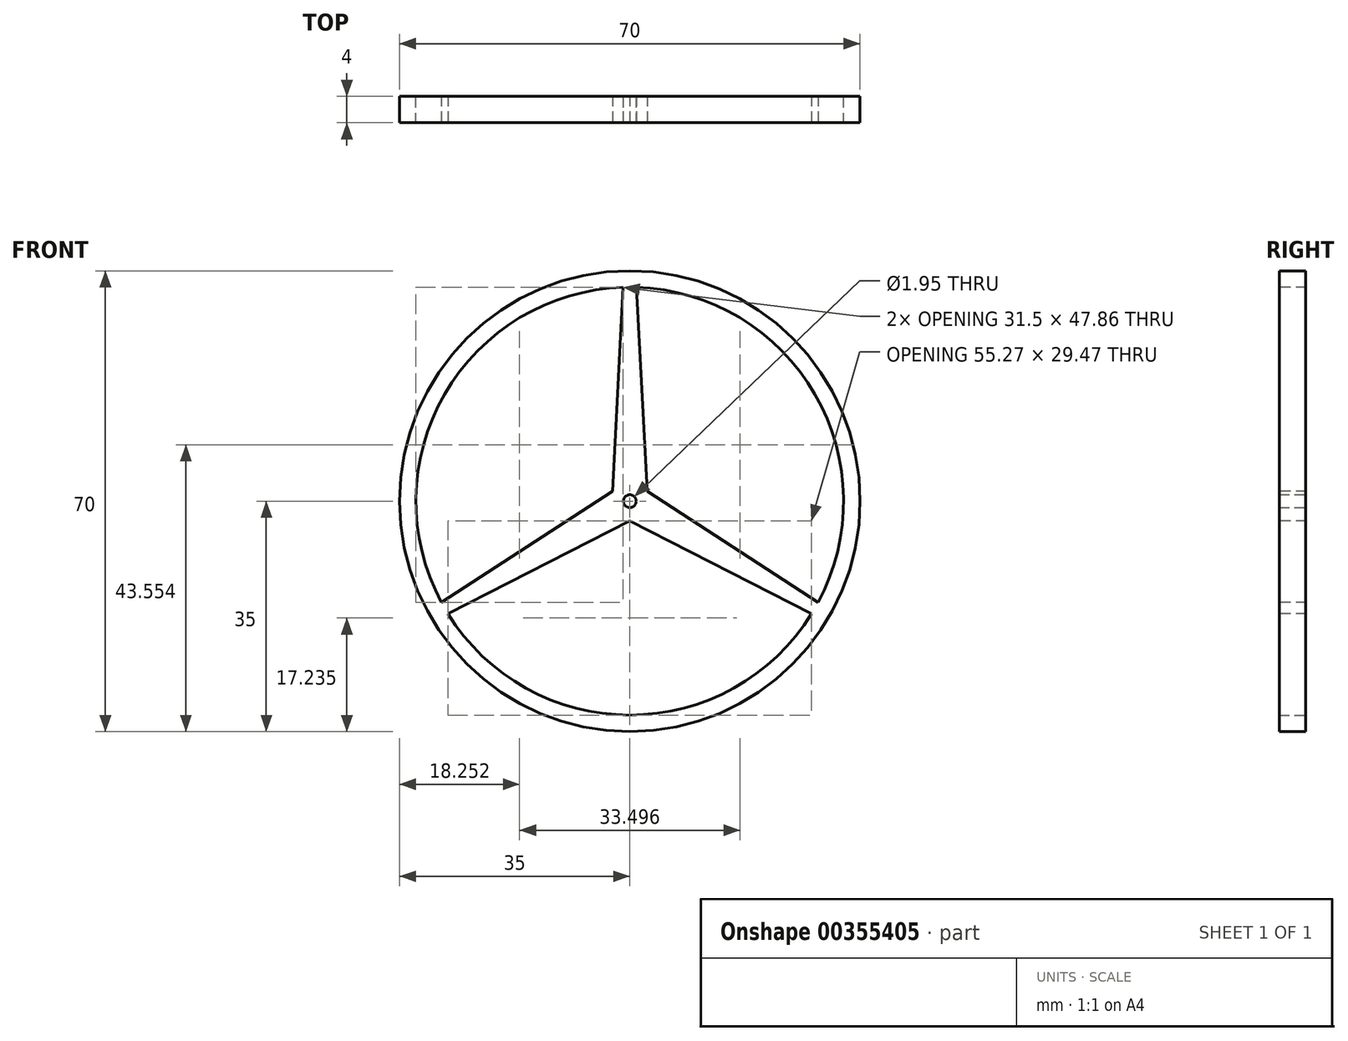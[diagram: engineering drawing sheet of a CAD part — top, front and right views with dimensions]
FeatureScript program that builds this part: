
annotation { "Feature Type Name" : "Feature", "Feature Type Description" : "" }
export const myFeature = defineFeature(function(context is Context, id is Id, definition is map)
    precondition{}
    {
        {
            var Q0;
            Q0=qCreatedBy(makeId("Front.planeOp"),FACE);
            var sketch = newSketch(context, id + "F0", { "sketchPlane" : qUnion([Q0])});
            skCircle(sketch, "E0", {"center": v(0, 0) * mm, "radius": 35 * mm});
            skCircle(sketch, "E1", {"center": v(0, 0) * mm, "radius": 0.97 * mm});
            skCircle(sketch, "E2", {"center": v(0, 0) * mm, "radius": 2.98 * mm});
            skCircle(sketch, "E3", {"center": v(0, 0) * mm, "radius": 32.5 * mm});
            skSolve(sketch);
        }
        {
            var Q0;
            Q0=qSketchRegion(id+"F0",true);
            var Q1;
            Q1=makeQuery(id+"F0.imprint","IMPRINT",FACE,{"disambiguationData":[TD([[makeQuery(id+"F0.imprint","IMPRINT",EDGE,{"derivedFrom":sQuery(id+"F0.wireOp",EDGE,"E1")}),-1.0]])]});
            extrude(context, id + "F1", {"entities" : qUnion([Q0, Q1]), "depth" : 4 * mm});
        }
        {
            var Q0;
            Q0=makeQuery(id+"F1.opExtrude","CAP_FACE",FACE,{"disambiguationData":[OSD([sQuery(id+"F0.wireOp",EDGE,"E0"),sQuery(id+"F0.wireOp",EDGE,"E3")])],"isStart":false});
            var sketch = newSketch(context, id + "F2", { "sketchPlane" : qUnion([Q0])});
            skLineSegment(sketch, "E4", {"start": v(1, 32.48) * mm, "end": v(2.63, 1.4) * mm});
            skLineSegment(sketch, "E5", {"start": v(-1, 32.48) * mm, "end": v(-2.63, 1.4) * mm});
            skLineSegment(sketch, "E6.1.0", {"start": v(-27.63, -17.1) * mm, "end": v(0.1, -2.97) * mm});
            skLineSegment(sketch, "E6.1.1", {"start": v(-28.63, -15.38) * mm, "end": v(-2.52, 1.58) * mm});
            skLineSegment(sketch, "E6.2.0", {"start": v(28.63, -15.38) * mm, "end": v(2.52, 1.58) * mm});
            skLineSegment(sketch, "E6.2.1", {"start": v(27.63, -17.1) * mm, "end": v(-0.1, -2.97) * mm});
            skPoint(sketch, "E6.center", {"position": v(0, 0) * mm});
            skArc(sketch, "E7", {"start": v(-28.63, -15.38) * mm, "mid": v(-28.15, -16.25) * mm, "end": v(-27.63, -17.1) * mm});
            skCircle(sketch, "E8", {"center": v(0, 0) * mm, "radius": 2.97 * mm});
            skArc(sketch, "E9.trimOffspring", {"start": v(1, 32.48) * mm, "mid": v(0, 32.5) * mm, "end": v(-1, 32.48) * mm});
            skArc(sketch, "E10.trimOffspring", {"start": v(27.63, -17.1) * mm, "mid": v(28.15, -16.25) * mm, "end": v(28.63, -15.38) * mm});
            skCircle(sketch, "E11", {"center": v(0, 0) * mm, "radius": 0.97 * mm});
            skSolve(sketch);
        }
        {
            var Q0;
            Q0=qSketchRegion(id+"F2",true);
            extrude(context, id + "F3", {"entities" : qUnion([Q0]), "operationType" : NewBodyOperationType.ADD, "oppositeDirection" : true, "depth" : 4 * mm});
        }
        {
            var Q0;
            Q0=qCreatedBy(makeId("Right.planeOp"),FACE);
            var sketch = newSketch(context, id + "F4", { "sketchPlane" : qUnion([Q0])});
            skLineSegment(sketch, "E12", {"start": v(2.14, 1.57) * mm, "end": v(5.63, 1.57) * mm});
            skLineSegment(sketch, "E13", {"start": v(5.63, 1.57) * mm, "end": v(5.63, 33.89) * mm});
            skLineSegment(sketch, "E14", {"start": v(5.63, 33.89) * mm, "end": v(0, 33.89) * mm});
            skLineSegment(sketch, "E15", {"start": v(0, 33.89) * mm, "end": v(0, 13) * mm});
            skLineSegment(sketch, "E16", {"start": v(-16.5, 0) * mm, "end": v(18.02, 0) * mm});
            skLineSegment(sketch, "E17", {"start": v(18.02, 0) * mm, "end": v(18.02, 0.48) * mm});
            skLineSegment(sketch, "E18", {"start": v(2.14, 1.57) * mm, "end": v(0, 32.53) * mm});
            skLineSegment(sketch, "E19", {"start": v(0, 32.53) * mm, "end": v(0, 33.89) * mm});
            skSolve(sketch);
        }
        {
            var Q0;
            Q0=qSketchRegion(id+"F4",true);
            var Q1;
            Q1=sQuery(id+"F4.wireOp",EDGE,"E16");
            revolve(context, id + "F5", {"operationType" : NewBodyOperationType.REMOVE, "entities" : qUnion([Q0]), "axis" : qUnion([Q1]), "revolveType" : RevolveType.FULL});
        }
    });
